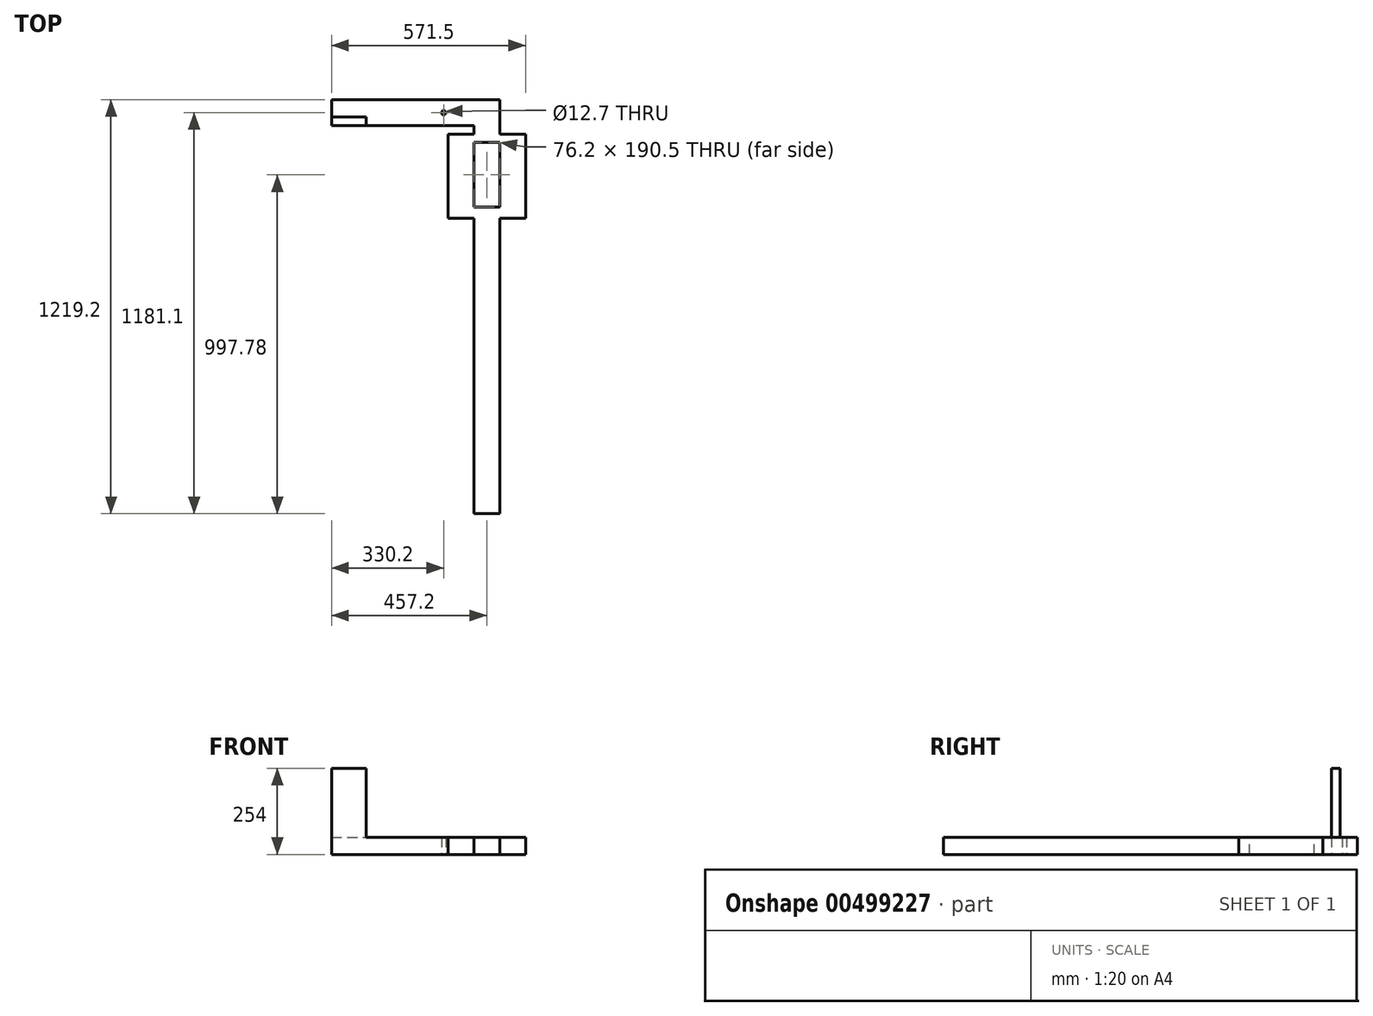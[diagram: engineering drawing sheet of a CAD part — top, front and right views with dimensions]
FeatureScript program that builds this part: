
annotation { "Feature Type Name" : "Feature", "Feature Type Description" : "" }
export const myFeature = defineFeature(function(context is Context, id is Id, definition is map)
    precondition{}
    {
        {
            var Q0;
            Q0=qCreatedBy(makeId("Top.planeOp"),FACE);
            var sketch = newSketch(context, id + "F0", { "sketchPlane" : qUnion([Q0])});
            skLineSegment(sketch, "E0.bottom", {"start": v(-247.65, 38.1) * mm, "end": v(247.65, 38.1) * mm});
            skLineSegment(sketch, "E0.top", {"start": v(-247.65, -38.1) * mm, "end": v(171.45, -38.1) * mm});
            skLineSegment(sketch, "E0.left", {"start": v(-247.65, 38.1) * mm, "end": v(-247.65, -38.1) * mm});
            skLineSegment(sketch, "E0.right", {"start": v(247.65, 38.1) * mm, "end": v(247.65, -38.1) * mm});
            skPoint(sketch, "E0.middle", {"position": v(0, 0) * mm});
            skLineSegment(sketch, "E1", {"start": v(247.65, 0) * mm, "end": v(-57.15, 0) * mm, "construction": true});
            skLineSegment(sketch, "E2", {"start": v(-57.15, 0) * mm, "end": v(-57.15, -19.17) * mm, "construction": true});
            skLineSegment(sketch, "E3", {"start": v(-57.15, -19.17) * mm, "end": v(120.65, -19.17) * mm, "construction": true});
            skPoint(sketch, "E4", {"position": v(120.65, 0) * mm});
            skLineSegment(sketch, "E5.left", {"start": v(247.65, -38.1) * mm, "end": v(247.65, -63.5) * mm});
            skLineSegment(sketch, "E5.right", {"start": v(171.45, -38.1) * mm, "end": v(171.45, -63.5) * mm});
            skLineSegment(sketch, "E6", {"start": v(120.65, 0) * mm, "end": v(120.65, -30.49) * mm, "construction": true});
            skLineSegment(sketch, "E7", {"start": v(247.65, 19.12) * mm, "end": v(82.55, 19.12) * mm, "construction": true});
            skPoint(sketch, "E8", {"position": v(82.55, 0) * mm});
            skCircle(sketch, "E9", {"center": v(82.55, 0) * mm, "radius": 6.35 * mm});
            skLineSegment(sketch, "E10", {"start": v(171.45, -63.5) * mm, "end": v(95.25, -63.5) * mm});
            skLineSegment(sketch, "E11", {"start": v(247.65, -63.5) * mm, "end": v(323.85, -63.5) * mm});
            skLineSegment(sketch, "E12", {"start": v(95.25, -63.5) * mm, "end": v(95.25, -311.15) * mm});
            skLineSegment(sketch, "E13", {"start": v(95.25, -311.15) * mm, "end": v(171.45, -311.15) * mm});
            skLineSegment(sketch, "E14", {"start": v(323.85, -63.5) * mm, "end": v(323.85, -311.15) * mm});
            skLineSegment(sketch, "E15", {"start": v(323.85, -311.15) * mm, "end": v(247.65, -311.15) * mm});
            skLineSegment(sketch, "E16.top", {"start": v(247.65, -1181.1) * mm, "end": v(171.45, -1181.1) * mm});
            skLineSegment(sketch, "E16.left", {"start": v(247.65, -311.15) * mm, "end": v(247.65, -1181.1) * mm});
            skLineSegment(sketch, "E16.right", {"start": v(171.45, -311.15) * mm, "end": v(171.45, -1181.1) * mm});
            skLineSegment(sketch, "E17", {"start": v(95.25, -70.67) * mm, "end": v(323.85, -70.67) * mm, "construction": true});
            skSolve(sketch);
        }
        {
            var Q0;
            Q0=makeQuery(id+"F0.imprint","IMPRINT",FACE,{"disambiguationData":[TD([[makeQuery(id+"F0.imprint","IMPRINT",EDGE,{"derivedFrom":sQuery(id+"F0.wireOp",EDGE,"E0.bottom")}),-1.0]])]});
            extrude(context, id + "F1", {"entities" : qUnion([Q0]), "depth" : 50.8 * mm, "offsetDistance" : 25.4 * mm});
        }
        {
            var Q0;
            Q0=makeQuery(id+"F1.opExtrude","CAP_FACE",FACE,{"disambiguationData":[OSD([sQuery(id+"F0.wireOp",EDGE,"E0.bottom"),sQuery(id+"F0.wireOp",EDGE,"E0.top"),sQuery(id+"F0.wireOp",EDGE,"E0.left"),sQuery(id+"F0.wireOp",EDGE,"E0.right"),sQuery(id+"F0.wireOp",EDGE,"BIq4sIMF-76BU-zMf5-rxe8-ENLJPPeP22kf"),sQuery(id+"F0.wireOp",EDGE,"E5.top"),sQuery(id+"F0.wireOp",EDGE,"E5.left"),sQuery(id+"F0.wireOp",EDGE,"E5.right")])],"isStart":false});
            var sketch = newSketch(context, id + "F2", { "sketchPlane" : qUnion([Q0])});
            skLineSegment(sketch, "E18.bottom", {"start": v(-247.65, -38.1) * mm, "end": v(-146.05, -38.1) * mm});
            skLineSegment(sketch, "E18.top", {"start": v(-247.65, -12.7) * mm, "end": v(-146.05, -12.7) * mm});
            skLineSegment(sketch, "E18.left", {"start": v(-247.65, -38.1) * mm, "end": v(-247.65, -12.7) * mm});
            skLineSegment(sketch, "E18.right", {"start": v(-146.05, -38.1) * mm, "end": v(-146.05, -12.7) * mm});
            skSolve(sketch);
        }
        {
            var Q0;
            Q0 = qSketchRegion(id + "F2", true);
            extrude(context, id + "F3", {"entities" : qUnion([Q0]), "operationType" : NewBodyOperationType.ADD, "depth" : 203.2 * mm, "offsetDistance" : 25.4 * mm});
        }
        {
            var Q0;
            Q0=makeQuery(id+"F1.opExtrude","CAP_FACE",FACE,{"disambiguationData":[OSD([sQuery(id+"F0.wireOp",EDGE,"E0.bottom"),sQuery(id+"F0.wireOp",EDGE,"E0.top"),sQuery(id+"F0.wireOp",EDGE,"E0.left"),sQuery(id+"F0.wireOp",EDGE,"E0.right"),sQuery(id+"F0.wireOp",EDGE,"E9"),sQuery(id+"F0.wireOp",EDGE,"E5.right"),sQuery(id+"F0.wireOp",EDGE,"E5.left"),sQuery(id+"F0.wireOp",EDGE,"E10"),sQuery(id+"F0.wireOp",EDGE,"E11"),sQuery(id+"F0.wireOp",EDGE,"E12"),sQuery(id+"F0.wireOp",EDGE,"E13"),sQuery(id+"F0.wireOp",EDGE,"E14"),sQuery(id+"F0.wireOp",EDGE,"E15"),sQuery(id+"F0.wireOp",EDGE,"E16.top"),sQuery(id+"F0.wireOp",EDGE,"E16.left"),sQuery(id+"F0.wireOp",EDGE,"E16.right")])],"isStart":false});
            var sketch = newSketch(context, id + "F4", { "sketchPlane" : qUnion([Q0])});
            skLineSegment(sketch, "E19.bottom", {"start": v(171.45, -88.07) * mm, "end": v(247.65, -88.07) * mm});
            skLineSegment(sketch, "E19.top", {"start": v(171.45, -278.57) * mm, "end": v(247.65, -278.57) * mm});
            skLineSegment(sketch, "E19.left", {"start": v(171.45, -88.07) * mm, "end": v(171.45, -278.57) * mm});
            skLineSegment(sketch, "E19.right", {"start": v(247.65, -88.07) * mm, "end": v(247.65, -278.57) * mm});
            skSolve(sketch);
        }
        {
            var Q0;
            Q0=makeQuery(id+"F4.imprint","IMPRINT",FACE,{"disambiguationData":[TD([[makeQuery(id+"F4.imprint","IMPRINT",EDGE,{"derivedFrom":sQuery(id+"F4.wireOp",EDGE,"E19.bottom")}),-1.0]])]});
            extrude(context, id + "F5", {"entities" : qUnion([Q0]), "operationType" : NewBodyOperationType.REMOVE, "oppositeDirection" : true, "depth" : 50.8 * mm, "offsetDistance" : 25.4 * mm});
        }
    });
